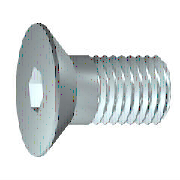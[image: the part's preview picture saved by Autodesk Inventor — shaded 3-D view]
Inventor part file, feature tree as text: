
AUTODESK INVENTOR PART (.ipt)
format: ipt  version: 2020 (Build 240168000, 168)  size: 177,152 bytes
history: native  units: mm (DEFAULTED — no unit token found)
features: sketch x2, extrude x1, plane x1
ambient origin geometry x7: Origin, YZ Plane, XY Plane, X Axis, Y Axis, Z Axis, Center Point
bodies: Solid1 (feature_tree), Body (feature_tree)
feature tree (4):
  sketch  "Sketch2"  dims[d2=1.5mm d3=4.0mm d6=2.48mm d7=45.0deg d8=2.886751mm d9=60.0deg d10=7.53mm d11=4.0mm d12=0.429415mm d13=90.0deg d30=10.0mm d14=0.0mm d15=20.0mm d16=0.0mm d17=0.429415mm d18=0.429415mm d20=0.0mm d39=45.0deg d43=0.0mm d44=0.0mm]
  extrude  "Slot"  Depth=20.0mm
  plane  "Work Plane1"
  sketch  "Sketch1"  dims[d0=40.0mm d1=20.0mm]
